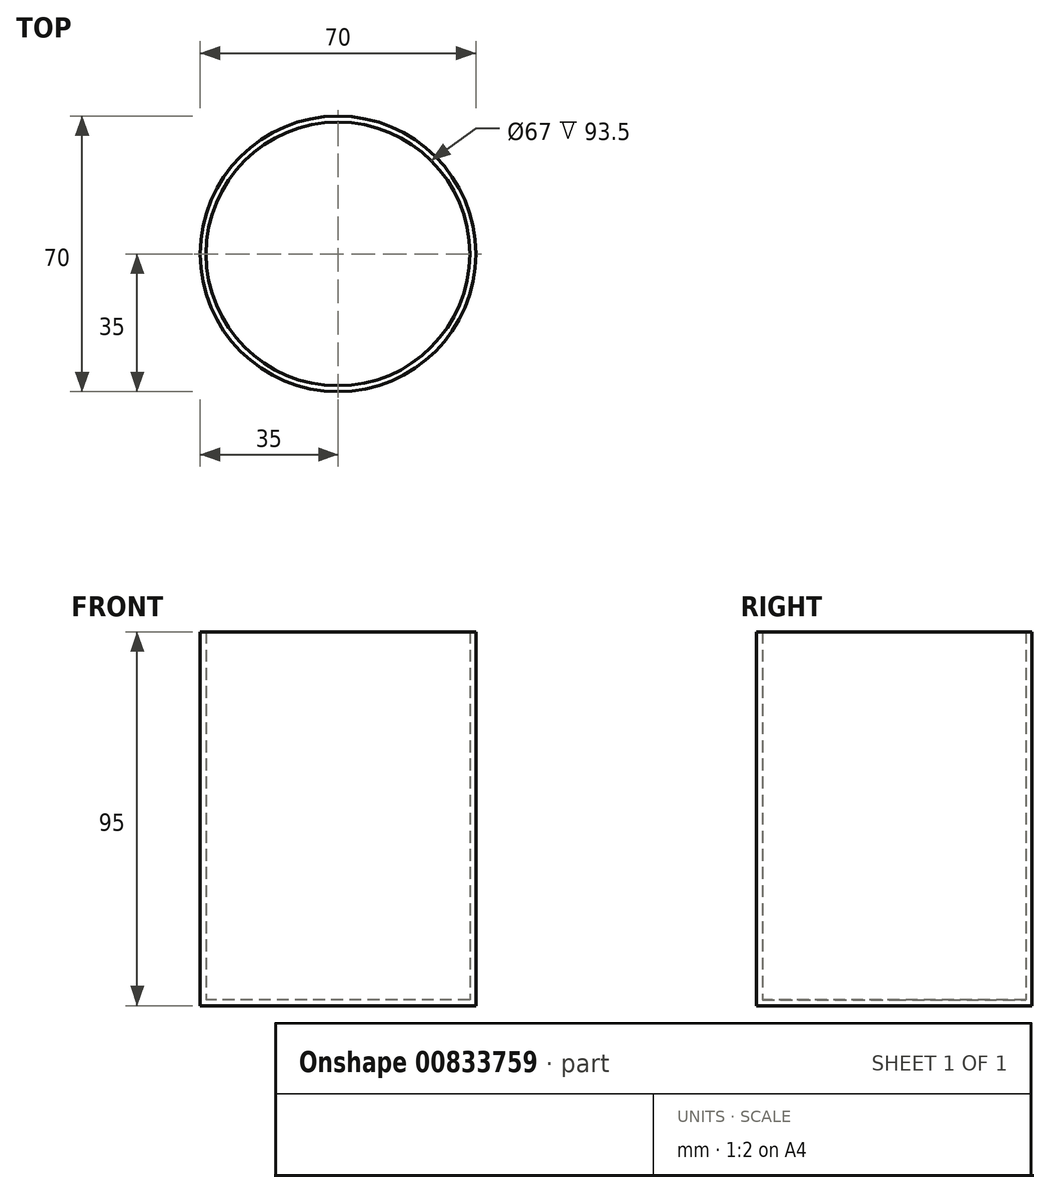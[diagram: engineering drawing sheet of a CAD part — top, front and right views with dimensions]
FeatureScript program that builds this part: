
annotation { "Feature Type Name" : "Feature", "Feature Type Description" : "" }
export const myFeature = defineFeature(function(context is Context, id is Id, definition is map)
    precondition{}
    {
        {
            var Q0;
            Q0=qCreatedBy(makeId("Top.planeOp"),FACE);
            var sketch = newSketch(context, id + "F0", { "sketchPlane" : qUnion([Q0])});
            skCircle(sketch, "E0", {"center": v(0, 0) * mm, "radius": 35 * mm});
            skSolve(sketch);
        }
        {
            var Q0;
            Q0 = qSketchRegion(id + "F0", true);
            extrude(context, id + "F1", {"entities" : qUnion([Q0]), "depth" : 95 * mm, "offsetDistance" : 25 * mm});
        }
        {
            var Q0;
            Q0=makeQuery(id+"F1.opExtrude","CAP_FACE",FACE,{"disambiguationData":[OSD([sQuery(id+"F0.wireOp",EDGE,"E0")])],"isStart":false});
            shell(context, id + "F2", {"entities" : qUnion([Q0]), "thickness" : 1.5 * mm});
        }
        {
            var Q0;
            Q0=qCreatedBy(makeId("Top.planeOp"),FACE);
            var sketch = newSketch(context, id + "F3", { "sketchPlane" : qUnion([Q0])});
            skCircle(sketch, "E1", {"center": v(0, 0) * mm, "radius": 35 * mm});
            skSolve(sketch);
        }
        {
            var Q0;
            Q0 = qSketchRegion(id + "F3", true);
            extrude(context, id + "F4", {"entities" : qUnion([Q0]), "operationType" : NewBodyOperationType.ADD, "depth" : 1.5 * mm, "offsetDistance" : 25 * mm});
        }
    });
